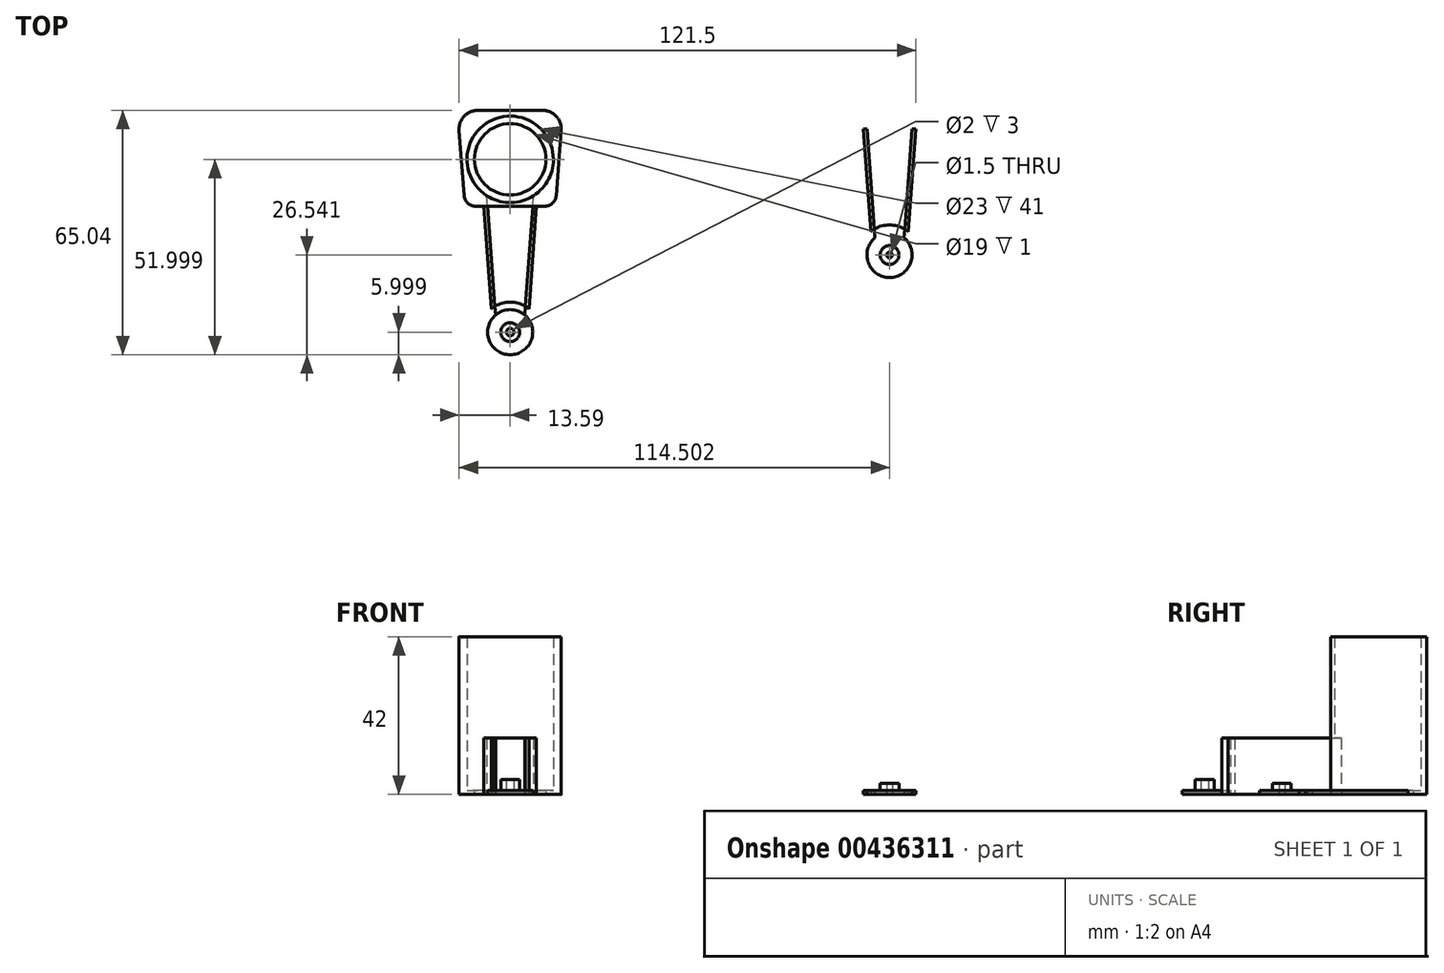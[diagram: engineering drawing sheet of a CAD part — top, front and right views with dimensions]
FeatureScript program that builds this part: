
annotation { "Feature Type Name" : "Feature", "Feature Type Description" : "" }
export const myFeature = defineFeature(function(context is Context, id is Id, definition is map)
    precondition{}
    {
        {
            var Q0;
            Q0=qCreatedBy(makeId("Top.planeOp"),FACE);
            var sketch = newSketch(context, id + "F0", { "sketchPlane" : qUnion([Q0])});
            skCircle(sketch, "E0", {"center": v(0, 24.88) * mm, "radius": 11.5 * mm});
            skCircle(sketch, "E1", {"center": v(0, -21.12) * mm, "radius": 6 * mm});
            skCircle(sketch, "E2", {"center": v(0, 24.88) * mm, "radius": 9.5 * mm});
            skCircle(sketch, "E3", {"center": v(0, -21.12) * mm, "radius": 8 * mm});
            skLineSegment(sketch, "E4", {"start": v(-8.6, 37.92) * mm, "end": v(8.6, 37.92) * mm});
            skLineSegment(sketch, "E5", {"start": v(13.58, 32.53) * mm, "end": v(12.22, 15.15) * mm});
            skLineSegment(sketch, "E6", {"start": v(9.23, 12.38) * mm, "end": v(-9.23, 12.38) * mm});
            skLineSegment(sketch, "E7", {"start": v(-12.22, 15.15) * mm, "end": v(-13.58, 32.53) * mm});
            skLineSegment(sketch, "E8", {"start": v(-7, 12.38) * mm, "end": v(-5, -14.88) * mm});
            skLineSegment(sketch, "E9", {"start": v(7, 12.38) * mm, "end": v(5, -14.88) * mm});
            skPoint(sketch, "E10.visualSharp", {"position": v(-14, 37.92) * mm});
            skArc(sketch, "E10.filletArc", {"start": v(-8.6, 37.92) * mm, "mid": v(-12.26, 36.32) * mm, "end": v(-13.58, 32.53) * mm});
            skPoint(sketch, "E11.visualSharp", {"position": v(14, 37.92) * mm});
            skArc(sketch, "E11.filletArc", {"start": v(13.58, 32.53) * mm, "mid": v(12.26, 36.32) * mm, "end": v(8.6, 37.92) * mm});
            skPoint(sketch, "E12.visualSharp", {"position": v(-12, 12.38) * mm});
            skArc(sketch, "E12.filletArc", {"start": v(-12.22, 15.15) * mm, "mid": v(-11.26, 13.18) * mm, "end": v(-9.23, 12.38) * mm});
            skPoint(sketch, "E13.visualSharp", {"position": v(12, 12.38) * mm});
            skArc(sketch, "E13.filletArc", {"start": v(9.23, 12.38) * mm, "mid": v(11.26, 13.18) * mm, "end": v(12.22, 15.15) * mm});
            skLineSegment(sketch, "E14", {"start": v(-6, 12.38) * mm, "end": v(-4.05, -14.22) * mm});
            skLineSegment(sketch, "E15", {"start": v(6, 12.38) * mm, "end": v(4.05, -14.22) * mm});
            skLineSegment(sketch, "E16", {"start": v(0, 24.88) * mm, "end": v(12.98, 24.88) * mm});
            skLineSegment(sketch, "E17", {"start": v(12.98, 24.88) * mm, "end": v(-12.98, 24.88) * mm});
            skLineSegment(sketch, "E18", {"start": v(-6, 12.38) * mm, "end": v(-3.88, -16.54) * mm});
            skLineSegment(sketch, "E19", {"start": v(6, 12.38) * mm, "end": v(3.88, -16.54) * mm});
            skLineSegment(sketch, "E20", {"start": v(-3.88, -16.54) * mm, "end": v(-6.2, 15.2) * mm});
            skLineSegment(sketch, "E21", {"start": v(3.88, -16.54) * mm, "end": v(6.2, 15.2) * mm});
            skCircle(sketch, "E22", {"center": v(0, -21.12) * mm, "radius": 2.5 * mm});
            skCircle(sketch, "E23", {"center": v(0, -21.12) * mm, "radius": 1 * mm});
            skCircle(sketch, "E24", {"center": v(100.91, 45.42) * mm, "radius": 11.5 * mm});
            skCircle(sketch, "E25", {"center": v(100.91, -0.58) * mm, "radius": 6 * mm});
            skCircle(sketch, "E26", {"center": v(100.91, 45.42) * mm, "radius": 9.5 * mm});
            skCircle(sketch, "E27", {"center": v(100.91, -0.58) * mm, "radius": 8 * mm});
            skLineSegment(sketch, "E28", {"start": v(92.32, 58.47) * mm, "end": v(109.5, 58.47) * mm});
            skLineSegment(sketch, "E29", {"start": v(114.49, 53.08) * mm, "end": v(113.13, 35.69) * mm});
            skLineSegment(sketch, "E30", {"start": v(110.14, 32.92) * mm, "end": v(91.69, 32.92) * mm});
            skLineSegment(sketch, "E31", {"start": v(88.7, 35.69) * mm, "end": v(87.33, 53.08) * mm});
            skLineSegment(sketch, "E32", {"start": v(93.91, 32.92) * mm, "end": v(95.91, 5.67) * mm});
            skLineSegment(sketch, "E33", {"start": v(107.91, 32.92) * mm, "end": v(105.91, 5.67) * mm});
            skPoint(sketch, "E34.visualSharp", {"position": v(86.91, 58.47) * mm});
            skArc(sketch, "E34.filletArc", {"start": v(92.32, 58.47) * mm, "mid": v(88.65, 56.86) * mm, "end": v(87.33, 53.08) * mm});
            skPoint(sketch, "E35.visualSharp", {"position": v(114.91, 58.47) * mm});
            skArc(sketch, "E35.filletArc", {"start": v(114.49, 53.08) * mm, "mid": v(113.18, 56.86) * mm, "end": v(109.5, 58.47) * mm});
            skPoint(sketch, "E36.visualSharp", {"position": v(88.91, 32.92) * mm});
            skArc(sketch, "E36.filletArc", {"start": v(88.7, 35.69) * mm, "mid": v(89.65, 33.72) * mm, "end": v(91.69, 32.92) * mm});
            skPoint(sketch, "E37.visualSharp", {"position": v(112.91, 32.92) * mm});
            skArc(sketch, "E37.filletArc", {"start": v(110.14, 32.92) * mm, "mid": v(112.17, 33.72) * mm, "end": v(113.13, 35.69) * mm});
            skLineSegment(sketch, "E38", {"start": v(94.91, 32.92) * mm, "end": v(96.87, 6.32) * mm});
            skLineSegment(sketch, "E39", {"start": v(106.9, 32.92) * mm, "end": v(104.96, 6.32) * mm});
            skLineSegment(sketch, "E40", {"start": v(100.91, 45.42) * mm, "end": v(113.9, 45.42) * mm});
            skLineSegment(sketch, "E41", {"start": v(113.9, 45.42) * mm, "end": v(87.93, 45.42) * mm});
            skLineSegment(sketch, "E42", {"start": v(94.91, 32.92) * mm, "end": v(97.04, 4) * mm});
            skLineSegment(sketch, "E43", {"start": v(106.9, 32.92) * mm, "end": v(104.79, 4) * mm});
            skLineSegment(sketch, "E44", {"start": v(97.04, 4) * mm, "end": v(94.7, 35.74) * mm});
            skLineSegment(sketch, "E45", {"start": v(104.79, 4) * mm, "end": v(107.12, 35.74) * mm});
            skCircle(sketch, "E46", {"center": v(100.91, -0.58) * mm, "radius": 2.5 * mm});
            skCircle(sketch, "E47", {"center": v(100.91, -0.58) * mm, "radius": 0.75 * mm});
            skSolve(sketch);
        }
        {
            var Q0;
            Q0=makeQuery(id+"F0.imprint","IMPRINT",FACE,{"disambiguationData":[TD([[makeQuery(id+"F0.imprint","IMPRINT",EDGE,{"derivedFrom":sQuery(id+"F0.wireOp",EDGE,"E4")}),-1.0]])]});
            var Q1;
            {var subQ4=sQuery(id+"F0.wireOp",EDGE,"E13.filletArc");Q1=makeQuery(id+"F0.imprint","IMPRINT",FACE,{"disambiguationData":[TD([[makeQuery(id+"F0.imprint","IMPRINT",EDGE,{"derivedFrom":subQ4}),1.0]])]});}
            var Q2;
            {var subQ0=sQuery(id+"F0.wireOp",EDGE,"E12.filletArc");Q2=makeQuery(id+"F0.imprint","IMPRINT",FACE,{"disambiguationData":[TD([[makeQuery(id+"F0.imprint","IMPRINT",EDGE,{"derivedFrom":subQ0}),1.0]])]});}
            extrude(context, id + "F1", {"entities" : qUnion([Q0, Q1, Q2]), "depth" : 42 * mm});
        }
        {
            var Q0;
            {var subQ0=sQuery(id+"F0.wireOp",EDGE,"E8");Q0=makeQuery(id+"F0.imprint","IMPRINT",FACE,{"disambiguationData":[TD([[makeQuery(id+"F0.imprint","IMPRINT",EDGE,{"derivedFrom":subQ0}),1.0]])]});}
            var Q1;
            {var subQ0=sQuery(id+"F0.wireOp",EDGE,"E9");Q1=makeQuery(id+"F0.imprint","IMPRINT",FACE,{"disambiguationData":[TD([[makeQuery(id+"F0.imprint","IMPRINT",EDGE,{"derivedFrom":subQ0}),-1.0]])]});}
            var Q2;
            {var subQ5=sQuery(id+"F0.wireOp",EDGE,"E20");var subQ7=sQuery(id+"F0.wireOp",EDGE,"E1");var subQ8=makeQuery(id+"F0.imprint","INTERSECT",VERTEX,{"derivedFrom":[subQ7,subQ5]});Q2=makeQuery(id+"F0.imprint","IMPRINT",FACE,{"disambiguationData":[TD([[makeQuery(id+"F0.imprint","IMPRINT",EDGE,{"disambiguationData":[TD([[subQ8,-1.0]])],"derivedFrom":subQ7}),-1.0]])]});}
            extrude(context, id + "F2", {"entities" : qUnion([Q0, Q1, Q2]), "operationType" : NewBodyOperationType.ADD, "depth" : 15 * mm});
        }
        {
            var Q0;
            {var subQ0=sQuery(id+"F0.wireOp",EDGE,"E20");var subQ1=sQuery(id+"F0.wireOp",EDGE,"E0");var subQ2=makeQuery(id+"F0.imprint","INTERSECT",VERTEX,{"derivedFrom":[subQ1,subQ0]});Q0=makeQuery(id+"F0.imprint","IMPRINT",FACE,{"disambiguationData":[TD([[makeQuery(id+"F0.imprint","IMPRINT",EDGE,{"disambiguationData":[TD([[subQ2,-1.0]])],"derivedFrom":subQ1}),-1.0]])]});}
            extrude(context, id + "F3", {"entities" : qUnion([Q0]), "operationType" : NewBodyOperationType.ADD, "depth" : 42 * mm});
        }
        {
            var Q0;
            {var subQ0=sQuery(id+"F0.wireOp",EDGE,"E20");var subQ1=sQuery(id+"F0.wireOp",EDGE,"E0");var subQ2=makeQuery(id+"F0.imprint","INTERSECT",VERTEX,{"derivedFrom":[subQ1,subQ0]});Q0=makeQuery(id+"F0.imprint","IMPRINT",FACE,{"disambiguationData":[TD([[makeQuery(id+"F0.imprint","IMPRINT",EDGE,{"disambiguationData":[TD([[subQ2,-1.0]])],"derivedFrom":subQ1}),-1.0]])]});}
            extrude(context, id + "F4", {"entities" : qUnion([Q0]), "operationType" : NewBodyOperationType.REMOVE, "depth" : 15 * mm});
        }
        {
            var Q0;
            {var subQ0=sQuery(id+"F0.wireOp",EDGE,"E0");var subQ7=makeQuery(id+"F0.imprint","INTERSECT",VERTEX,{"derivedFrom":[subQ0,sQuery(id+"F0.wireOp",EDGE,"E20")]});Q0=makeQuery(id+"F0.imprint","IMPRINT",FACE,{"disambiguationData":[TD([[makeQuery(id+"F0.imprint","IMPRINT",EDGE,{"disambiguationData":[TD([[subQ7,1.0]])],"derivedFrom":subQ0}),1.0]])]});}
            var Q1;
            {var subQ0=sQuery(id+"F0.wireOp",EDGE,"E17");var subQ4=makeQuery(id+"F0.imprint","IMPRINT",VERTEX,{"derivedFrom":subQ0});Q1=makeQuery(id+"F0.imprint","IMPRINT",FACE,{"disambiguationData":[TD([[makeQuery(id+"F0.imprint","IMPRINT",EDGE,{"disambiguationData":[TD([[subQ4,1.0]])],"derivedFrom":subQ0}),1.0]])]});}
            var Q2;
            {var subQ0=sQuery(id+"F0.wireOp",EDGE,"E17");var subQ4=makeQuery(id+"F0.imprint","IMPRINT",VERTEX,{"derivedFrom":subQ0});Q2=makeQuery(id+"F0.imprint","IMPRINT",FACE,{"disambiguationData":[TD([[makeQuery(id+"F0.imprint","IMPRINT",EDGE,{"disambiguationData":[TD([[subQ4,1.0]])],"derivedFrom":subQ0}),-1.0]])]});}
            var Q3;
            {var subQ0=sQuery(id+"F0.wireOp",EDGE,"E17");var subQ1=sQuery(id+"F0.wireOp",EDGE,"E0");var subQ2=makeQuery(id+"F0.imprint","INTERSECT",VERTEX,{"disambiguationData":[OD(0.0)],"derivedFrom":[subQ1,subQ0]});Q3=makeQuery(id+"F0.imprint","IMPRINT",FACE,{"disambiguationData":[TD([[makeQuery(id+"F0.imprint","IMPRINT",EDGE,{"disambiguationData":[TD([[subQ2,1.0]])],"derivedFrom":subQ1}),1.0]])]});}
            extrude(context, id + "F5", {"entities" : qUnion([Q0, Q1, Q2, Q3]), "operationType" : NewBodyOperationType.ADD, "depth" : 1 * mm});
        }
        {
            var Q0;
            {var subQ0=sQuery(id+"F0.wireOp",EDGE,"E21");var subQ1=sQuery(id+"F0.wireOp",EDGE,"E3");var subQ2=makeQuery(id+"F0.imprint","INTERSECT",VERTEX,{"derivedFrom":[subQ1,subQ0]});Q0=makeQuery(id+"F0.imprint","IMPRINT",FACE,{"disambiguationData":[TD([[makeQuery(id+"F0.imprint","IMPRINT",EDGE,{"disambiguationData":[TD([[subQ2,-1.0]])],"derivedFrom":subQ1}),-1.0]])]});}
            var Q1;
            Q1=makeQuery(id+"F0.imprint","IMPRINT",FACE,{"disambiguationData":[TD([[makeQuery(id+"F0.imprint","IMPRINT",EDGE,{"derivedFrom":sQuery(id+"F0.wireOp",EDGE,"E22")}),-1.0]])]});
            var Q2;
            {var subQ0=sQuery(id+"F0.wireOp",EDGE,"E20");var subQ1=sQuery(id+"F0.wireOp",EDGE,"E1");var subQ2=makeQuery(id+"F0.imprint","INTERSECT",VERTEX,{"derivedFrom":[subQ1,subQ0]});Q2=makeQuery(id+"F0.imprint","IMPRINT",FACE,{"disambiguationData":[TD([[makeQuery(id+"F0.imprint","IMPRINT",EDGE,{"disambiguationData":[TD([[subQ2,1.0]])],"derivedFrom":subQ1}),-1.0]])]});}
            var Q3;
            {var subQ0=sQuery(id+"F0.wireOp",EDGE,"E20");var subQ1=sQuery(id+"F0.wireOp",EDGE,"E0");var subQ2=makeQuery(id+"F0.imprint","INTERSECT",VERTEX,{"derivedFrom":[subQ1,subQ0]});Q3=makeQuery(id+"F0.imprint","IMPRINT",FACE,{"disambiguationData":[TD([[makeQuery(id+"F0.imprint","IMPRINT",EDGE,{"disambiguationData":[TD([[subQ2,-1.0]])],"derivedFrom":subQ1}),-1.0]])]});}
            extrude(context, id + "F6", {"entities" : qUnion([Q0, Q1, Q2, Q3]), "operationType" : NewBodyOperationType.ADD, "depth" : 1 * mm});
        }
        {
            var Q0;
            Q0=makeQuery(id+"F0.imprint","IMPRINT",FACE,{"disambiguationData":[TD([[makeQuery(id+"F0.imprint","IMPRINT",EDGE,{"derivedFrom":sQuery(id+"F0.wireOp",EDGE,"E22")}),1.0]])]});
            extrude(context, id + "F7", {"entities" : qUnion([Q0]), "operationType" : NewBodyOperationType.ADD, "depth" : 4 * mm});
        }
        {
            var Q0;
            Q0=makeQuery(id+"F0.imprint","IMPRINT",FACE,{"disambiguationData":[TD([[makeQuery(id+"F0.imprint","IMPRINT",EDGE,{"derivedFrom":sQuery(id+"F0.wireOp",EDGE,"E23")}),1.0]])]});
            extrude(context, id + "F8", {"entities" : qUnion([Q0]), "operationType" : NewBodyOperationType.ADD, "depth" : 1 * mm});
        }
        {
            var Q0;
            {var subQ0=sQuery(id+"F0.wireOp",EDGE,"E32");Q0=makeQuery(id+"F0.imprint","IMPRINT",FACE,{"disambiguationData":[TD([[makeQuery(id+"F0.imprint","IMPRINT",EDGE,{"derivedFrom":subQ0}),1.0]])]});}
            var Q1;
            {var subQ0=sQuery(id+"F0.wireOp",EDGE,"E33");Q1=makeQuery(id+"F0.imprint","IMPRINT",FACE,{"disambiguationData":[TD([[makeQuery(id+"F0.imprint","IMPRINT",EDGE,{"derivedFrom":subQ0}),-1.0]])]});}
            var Q2;
            {var subQ0=sQuery(id+"F0.wireOp",EDGE,"E45");var subQ1=sQuery(id+"F0.wireOp",EDGE,"E27");var subQ2=makeQuery(id+"F0.imprint","INTERSECT",VERTEX,{"derivedFrom":[subQ1,subQ0]});Q2=makeQuery(id+"F0.imprint","IMPRINT",FACE,{"disambiguationData":[TD([[makeQuery(id+"F0.imprint","IMPRINT",EDGE,{"disambiguationData":[TD([[subQ2,-1.0]])],"derivedFrom":subQ1}),-1.0]])]});}
            var Q3;
            {var subQ0=sQuery(id+"F0.wireOp",EDGE,"E44");var subQ1=sQuery(id+"F0.wireOp",EDGE,"E25");var subQ2=makeQuery(id+"F0.imprint","INTERSECT",VERTEX,{"derivedFrom":[subQ1,subQ0]});Q3=makeQuery(id+"F0.imprint","IMPRINT",FACE,{"disambiguationData":[TD([[makeQuery(id+"F0.imprint","IMPRINT",EDGE,{"disambiguationData":[TD([[subQ2,1.0]])],"derivedFrom":subQ1}),-1.0]])]});}
            var Q4;
            {var subQ5=sQuery(id+"F0.wireOp",EDGE,"E44");var subQ7=sQuery(id+"F0.wireOp",EDGE,"E25");var subQ8=makeQuery(id+"F0.imprint","INTERSECT",VERTEX,{"derivedFrom":[subQ7,subQ5]});Q4=makeQuery(id+"F0.imprint","IMPRINT",FACE,{"disambiguationData":[TD([[makeQuery(id+"F0.imprint","IMPRINT",EDGE,{"disambiguationData":[TD([[subQ8,-1.0]])],"derivedFrom":subQ7}),-1.0]])]});}
            var Q5;
            Q5=makeQuery(id+"F0.imprint","IMPRINT",FACE,{"disambiguationData":[TD([[makeQuery(id+"F0.imprint","IMPRINT",EDGE,{"derivedFrom":sQuery(id+"F0.wireOp",EDGE,"E46")}),-1.0]])]});
            extrude(context, id + "F9", {"entities" : qUnion([Q0, Q1, Q2, Q3, Q4, Q5]), "depth" : 1 * mm});
        }
        {
            var Q0;
            Q0=makeQuery(id+"F0.imprint","IMPRINT",FACE,{"disambiguationData":[TD([[makeQuery(id+"F0.imprint","IMPRINT",EDGE,{"derivedFrom":sQuery(id+"F0.wireOp",EDGE,"E46")}),1.0]])]});
            extrude(context, id + "F10", {"entities" : qUnion([Q0]), "operationType" : NewBodyOperationType.ADD, "depth" : 3 * mm});
        }
    });
